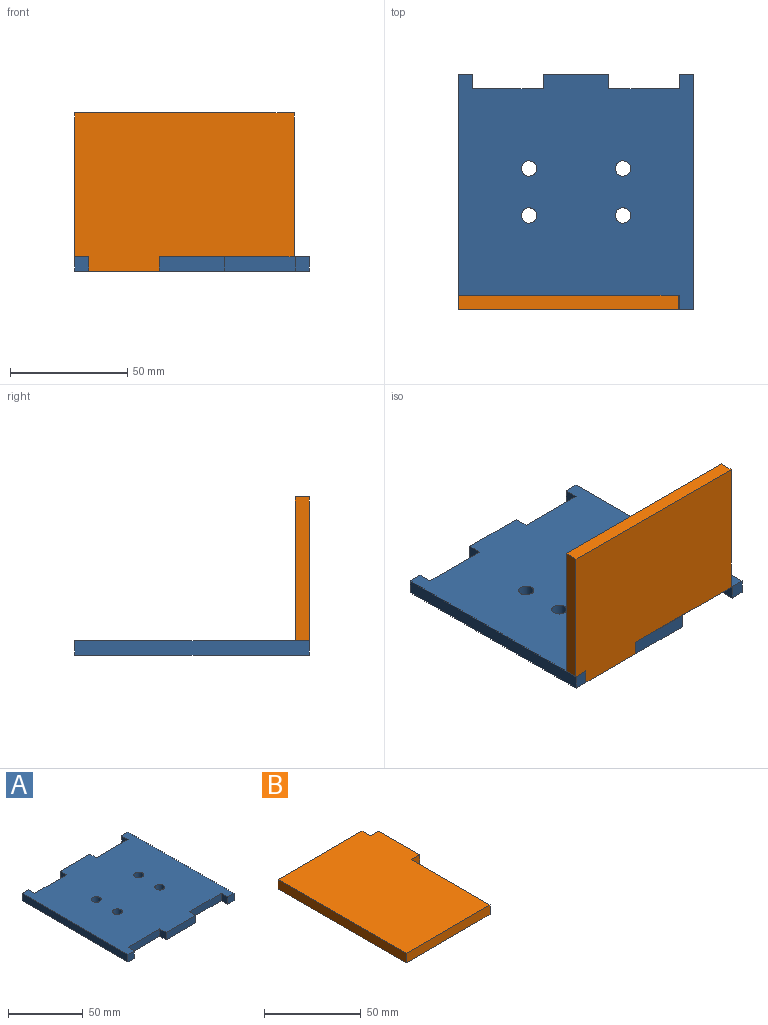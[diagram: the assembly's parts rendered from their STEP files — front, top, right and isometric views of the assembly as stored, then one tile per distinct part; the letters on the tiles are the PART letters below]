
ASSEMBLY  parts=2 mates=1
PART A: 26 faces, bbox 100x100x6 mm
  f0: plane 6x6mm, normal (-1,0,0), area 36mm2, adj f1,f22,f24,f25
  f1: plane 30x6mm, normal (0,1,0), area 180mm2, adj f0,f2,f24,f25
  f2: plane 6x6mm, normal (1,0,0), area 36mm2, adj f1,f3,f24,f25
  f3: plane 6x6mm, normal (0,1,0), area 36mm2, adj f2,f4,f24,f25
  f4: plane 100x6mm, normal (-1,0,0), area 600mm2, adj f3,f5,f24,f25
  f5: plane 6x6mm, normal (0,-1,0), area 36mm2, adj f4,f6,f24,f25
  f6: plane 6x6mm, normal (1,0,0), area 36mm2, adj f5,f7,f24,f25
  f7: plane 30x6mm, normal (0,-1,0), area 180mm2, adj f6,f8,f24,f25
  f8: plane 6x6mm, normal (-1,0,0), area 36mm2, adj f7,f9,f24,f25
  f9: plane 28x6mm, normal (0,-1,0), area 168mm2, adj f8,f10,f24,f25
  f10: plane 6x6mm, normal (1,0,0), area 36mm2, adj f9,f11,f24,f25
  f11: plane 30x6mm, normal (0,-1,0), area 180mm2, adj f10,f12,f24,f25
  f12: plane 6x6mm, normal (-1,0,0), area 36mm2, adj f11,f13,f24,f25
  f13: plane 6x6mm, normal (0,-1,0), area 36mm2, adj f12,f14,f24,f25
  f14: plane 100x6mm, normal (1,0,0), area 600mm2, adj f13,f15,f24,f25
  f15: plane 6x6mm, normal (0,1,0), area 36mm2, adj f14,f16,f24,f25
  f16: plane 6x6mm, normal (-1,0,0), area 36mm2, adj f15,f17,f24,f25
  f17: plane 30x6mm, normal (0,1,0), area 180mm2, adj f16,f18,f24,f25
  f18: plane 6x6mm, normal (1,0,0), area 36mm2, adj f17,f22,f24,f25
  f19: cylinder r=3.26mm len=6.51mm, axis (0,0,-1), area 122.8mm2, adj f24,f25
  f20: cylinder r=3.26mm len=6.51mm, axis (0,0,-1), area 122.8mm2, adj f24,f25
  f21: cylinder r=3.26mm len=6.51mm, axis (0,0,-1), area 122.8mm2, adj f24,f25
  f22: plane 28x6mm, normal (0,1,0), area 168mm2, adj f0,f18,f24,f25
  f23: cylinder r=3.26mm len=6.51mm, axis (0,0,-1), area 122.8mm2, adj f24,f25
  f24: plane 100x100mm, normal (0,0,1), area 9146.7mm2, adj f0,f1,f2,f3,f4,f5,f6,f7
  f25: plane 100x100mm, normal (0,0,-1), area 9146.7mm2, adj f0,f1,f2,f3,f4,f5,f6,f7
PART B: 10 faces, bbox 67.3x93.5x6 mm
  f0: plane 61.32x6mm, normal (0,1,0), area 367.9mm2, adj f1,f7,f8,f9
  f1: plane 93.46x6mm, normal (-1,0,0), area 560.8mm2, adj f0,f2,f8,f9
  f2: plane 61.32x6mm, normal (0,-1,0), area 367.9mm2, adj f1,f3,f8,f9
  f3: plane 57.46x6mm, normal (1,0,0), area 344.8mm2, adj f2,f4,f8,f9
  f4: plane 6x6mm, normal (0,-1,0), area 36mm2, adj f3,f5,f8,f9
  f5: plane 30x6mm, normal (1,0,0), area 180mm2, adj f4,f6,f8,f9
  f6: plane 6x6mm, normal (0,1,0), area 36mm2, adj f5,f7,f8,f9
  f7: plane 6x6mm, normal (1,0,0), area 36mm2, adj f0,f6,f8,f9
  f8: plane 93.46x67.32mm, normal (0,0,1), area 5911.3mm2, adj f0,f1,f2,f3,f4,f5,f6,f7
  f9: plane 93.46x67.32mm, normal (0,0,-1), area 5911.3mm2, adj f0,f1,f2,f3,f4,f5,f6,f7
PLACE A t=(-6.12,-29.62,12.26)mm
PLACE B rot(axis=(-0.58,0.58,0.58),120deg) t=(77.76,-22.88,-37.92)mm
MATE fastened B.f8 <-> A.f7  axis (0,1,0) through (-14.64,-16.88,18.26)mm
